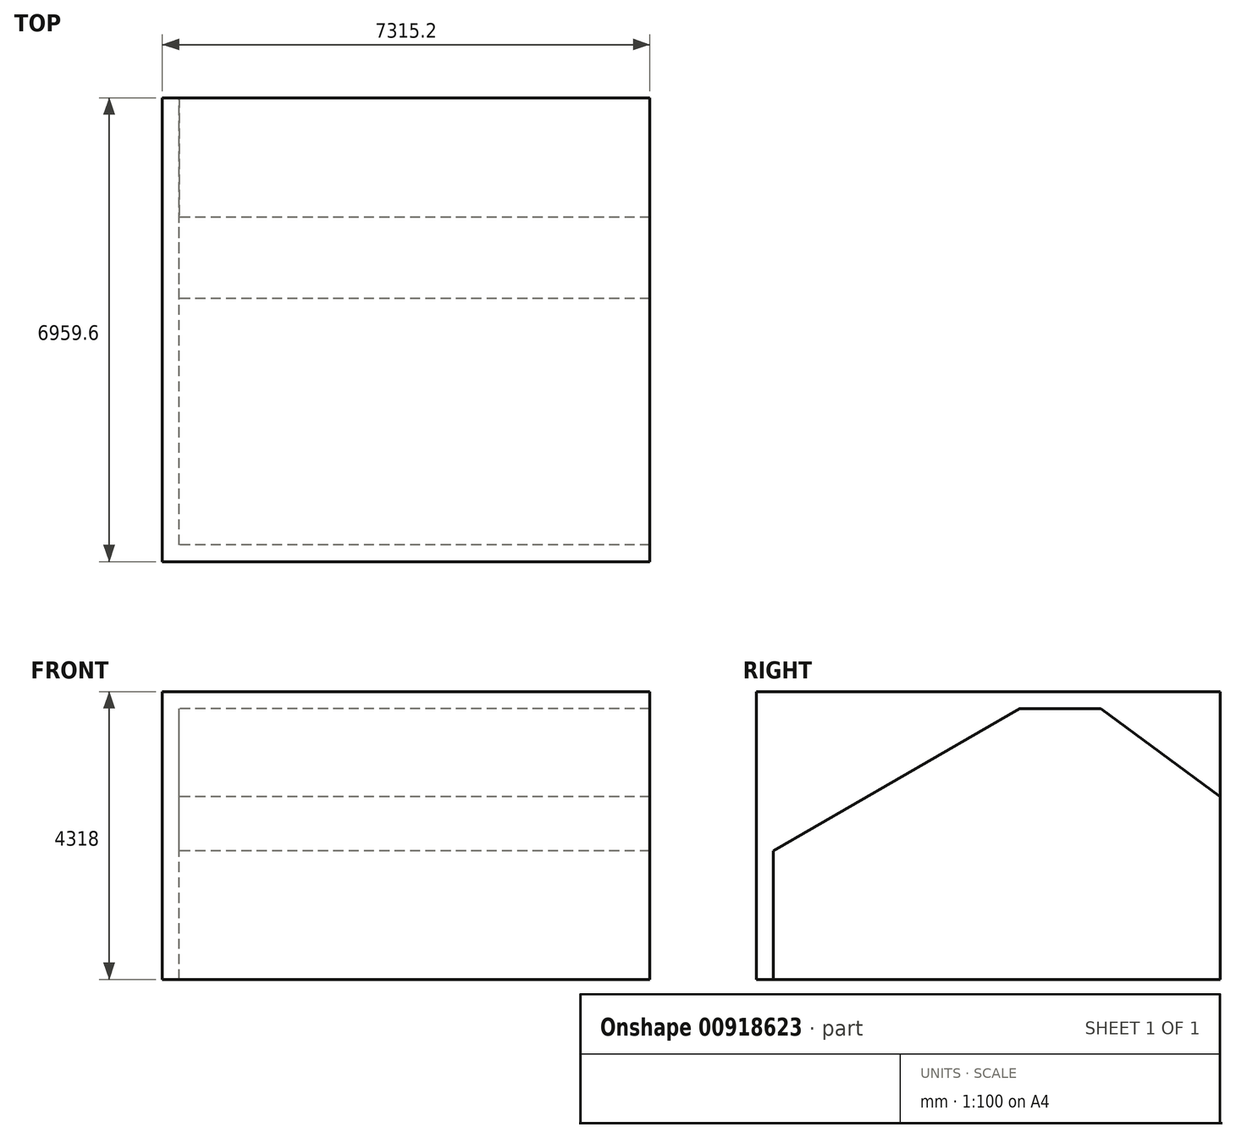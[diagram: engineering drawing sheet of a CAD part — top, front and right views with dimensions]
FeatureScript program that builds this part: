
annotation { "Feature Type Name" : "Feature", "Feature Type Description" : "" }
export const myFeature = defineFeature(function(context is Context, id is Id, definition is map)
    precondition{}
    {
        {
            var Q0;
            Q0=qCreatedBy(makeId("Right.planeOp"),FACE);
            var sketch = newSketch(context, id + "F0", { "sketchPlane" : qUnion([Q0])});
            skLineSegment(sketch, "E0", {"start": v(0, 0) * mm, "end": v(0, 1930.4) * mm});
            skLineSegment(sketch, "E1", {"start": v(0, 1930.4) * mm, "end": v(3695.5, 4064) * mm});
            skLineSegment(sketch, "E2", {"start": v(3695.5, 4064) * mm, "end": v(4914.7, 4064) * mm});
            skLineSegment(sketch, "E3", {"start": v(6959.6, 4318) * mm, "end": v(-254, 4318) * mm});
            skLineSegment(sketch, "E4", {"start": v(-254, 4318) * mm, "end": v(-254, 0) * mm});
            skLineSegment(sketch, "E5", {"start": v(-254, 0) * mm, "end": v(0, 0) * mm});
            skLineSegment(sketch, "E6", {"start": v(6959.6, 4318) * mm, "end": v(6959.6, 0) * mm});
            skLineSegment(sketch, "E7", {"start": v(6959.6, 0) * mm, "end": v(6705.6, 0) * mm});
            skLineSegment(sketch, "E8", {"start": v(6705.6, 0) * mm, "end": v(6705.6, 2743.2) * mm});
            skLineSegment(sketch, "E9", {"start": v(6705.6, 2743.2) * mm, "end": v(4914.7, 4064) * mm});
            skSolve(sketch);
        }
        {
            var Q0;
            Q0=makeQuery(id+"F0.imprint","IMPRINT",FACE,{"disambiguationData":[TD([[makeQuery(id+"F0.imprint","IMPRINT",EDGE,{"derivedFrom":sQuery(id+"F0.wireOp",EDGE,"E0")}),1.0]])]});
            extrude(context, id + "F1", {"entities" : qUnion([Q0]), "depth" : 7315.2 * mm, "offsetDistance" : 25.4 * mm});
        }
        {
            var Q0;
            Q0=makeQuery(id+"F1.opExtrude","CAP_FACE",FACE,{"disambiguationData":[OSD([sQuery(id+"F0.wireOp",EDGE,"E0"),sQuery(id+"F0.wireOp",EDGE,"E1"),sQuery(id+"F0.wireOp",EDGE,"E2"),sQuery(id+"F0.wireOp",EDGE,"q5zstEzm-i5na-q4YC-vvpk-Mn9zIfAN18yy"),sQuery(id+"F0.wireOp",EDGE,"E3"),sQuery(id+"F0.wireOp",EDGE,"E4"),sQuery(id+"F0.wireOp",EDGE,"E5")])],"isStart":true});
            var sketch = newSketch(context, id + "F2", { "sketchPlane" : qUnion([Q0])});
            skLineSegment(sketch, "E10.bottom", {"start": v(254, 4318) * mm, "end": v(-6959.6, 4318) * mm});
            skLineSegment(sketch, "E10.top", {"start": v(254, 0) * mm, "end": v(-6959.6, 0) * mm});
            skLineSegment(sketch, "E10.left", {"start": v(254, 4318) * mm, "end": v(254, 0) * mm});
            skLineSegment(sketch, "E10.right", {"start": v(-6959.6, 4318) * mm, "end": v(-6959.6, 0) * mm});
            skSolve(sketch);
        }
        {
            var Q0;
            {var subQ4=makeQuery(id+"F1.opExtrude","CAP_EDGE",EDGE,{"disambiguationData":[OSD([sQuery(id+"F0.wireOp",EDGE,"E0")])],"isStart":true});Q0=makeQuery(id+"F2.imprint","IMPRINT",FACE,{"disambiguationData":[TD([[makeQuery(id+"F2.imprint","IMPRINT",EDGE,{"derivedFrom":subQ4}),1.0]])]});}
            extrude(context, id + "F3", {"entities" : qUnion([Q0]), "operationType" : NewBodyOperationType.ADD, "oppositeDirection" : true, "depth" : 254 * mm, "offsetDistance" : 25.4 * mm});
        }
        {
            var Q0;
            Q0=makeQuery(id+"F1.opExtrude","CAP_FACE",FACE,{"disambiguationData":[OSD([sQuery(id+"F0.wireOp",EDGE,"E0"),sQuery(id+"F0.wireOp",EDGE,"E1"),sQuery(id+"F0.wireOp",EDGE,"E2"),sQuery(id+"F0.wireOp",EDGE,"E3"),sQuery(id+"F0.wireOp",EDGE,"E4"),sQuery(id+"F0.wireOp",EDGE,"E5"),sQuery(id+"F0.wireOp",EDGE,"E6"),sQuery(id+"F0.wireOp",EDGE,"E7"),sQuery(id+"F0.wireOp",EDGE,"E8"),sQuery(id+"F0.wireOp",EDGE,"E9")])],"isStart":false});
            var sketch = newSketch(context, id + "F4", { "sketchPlane" : qUnion([Q0])});
            skLineSegment(sketch, "E11", {"start": v(6705.6, 0) * mm, "end": v(6959.6, 0) * mm});
            skLineSegment(sketch, "E12", {"start": v(6959.6, 0) * mm, "end": v(6959.6, 4318) * mm});
            skLineSegment(sketch, "E13", {"start": v(6959.6, 4318) * mm, "end": v(6705.6, 4318) * mm});
            skLineSegment(sketch, "E14", {"start": v(6705.6, 4318) * mm, "end": v(6705.6, 0) * mm});
            skSolve(sketch);
        }
        {
            var Q0;
            {var subQ3=sQuery(id+"F4.wireOp",EDGE,"E11");Q0=makeQuery(id+"F4.imprint","IMPRINT",FACE,{"disambiguationData":[TD([[makeQuery(id+"F4.imprint","IMPRINT",EDGE,{"derivedFrom":subQ3}),-1.0]])]});}
            extrude(context, id + "F5", {"entities" : qUnion([Q0]), "operationType" : NewBodyOperationType.REMOVE, "endBound" : BoundingType.THROUGH_ALL, "oppositeDirection" : true, "depth" : 25.4 * mm, "offsetDistance" : 25.4 * mm});
        }
    });
